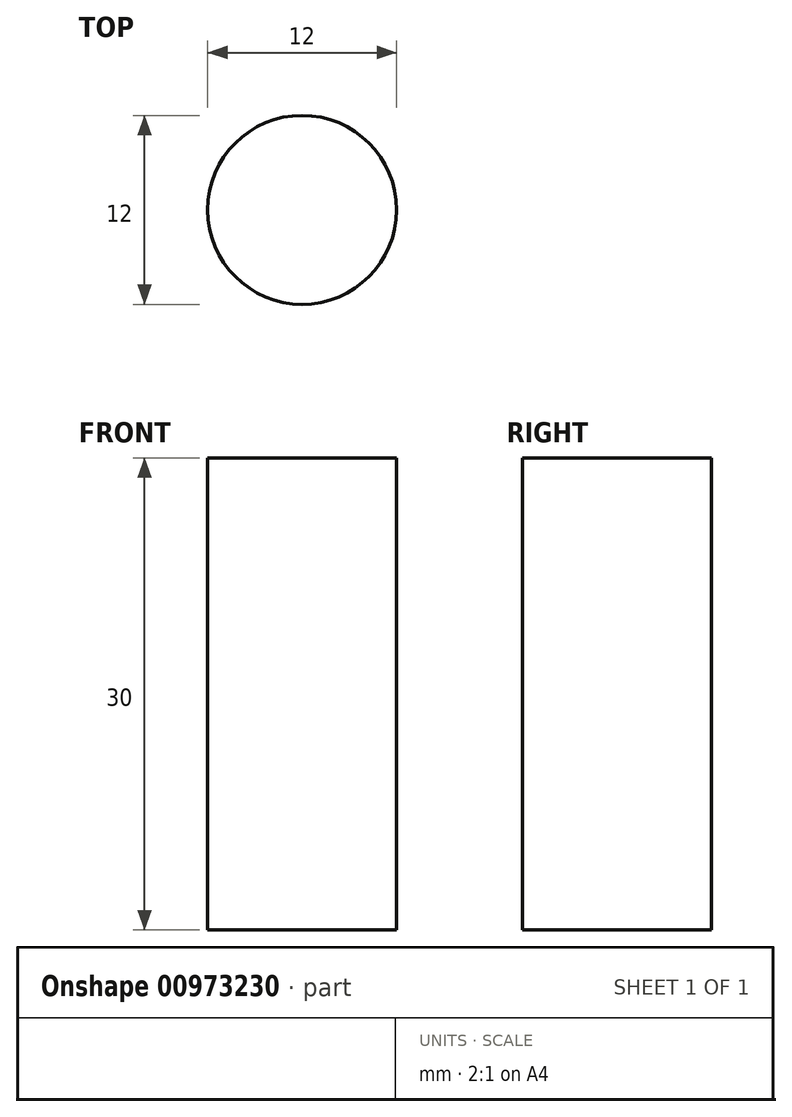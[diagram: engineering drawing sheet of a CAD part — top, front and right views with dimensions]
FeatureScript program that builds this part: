
annotation { "Feature Type Name" : "Feature", "Feature Type Description" : "" }
export const myFeature = defineFeature(function(context is Context, id is Id, definition is map)
    precondition{}
    {
        {
            var Q0;
            Q0=qCreatedBy(makeId("Top.planeOp"),FACE);
            var sketch = newSketch(context, id + "F0", { "sketchPlane" : qUnion([Q0])});
            skCircle(sketch, "E0", {"center": v(0, 0) * mm, "radius": 6 * mm});
            skSolve(sketch);
        }
        {
            var Q0;
            Q0=makeQuery(id+"F0.imprint","IMPRINT",FACE,{"disambiguationData":[TD([[makeQuery(id+"F0.imprint","IMPRINT",EDGE,{"derivedFrom":sQuery(id+"F0.wireOp",EDGE,"E0")}),1.0]])]});
            extrude(context, id + "F1", {"entities" : qUnion([Q0]), "depth" : 30 * mm, "offsetDistance" : 25 * mm});
        }
    });
